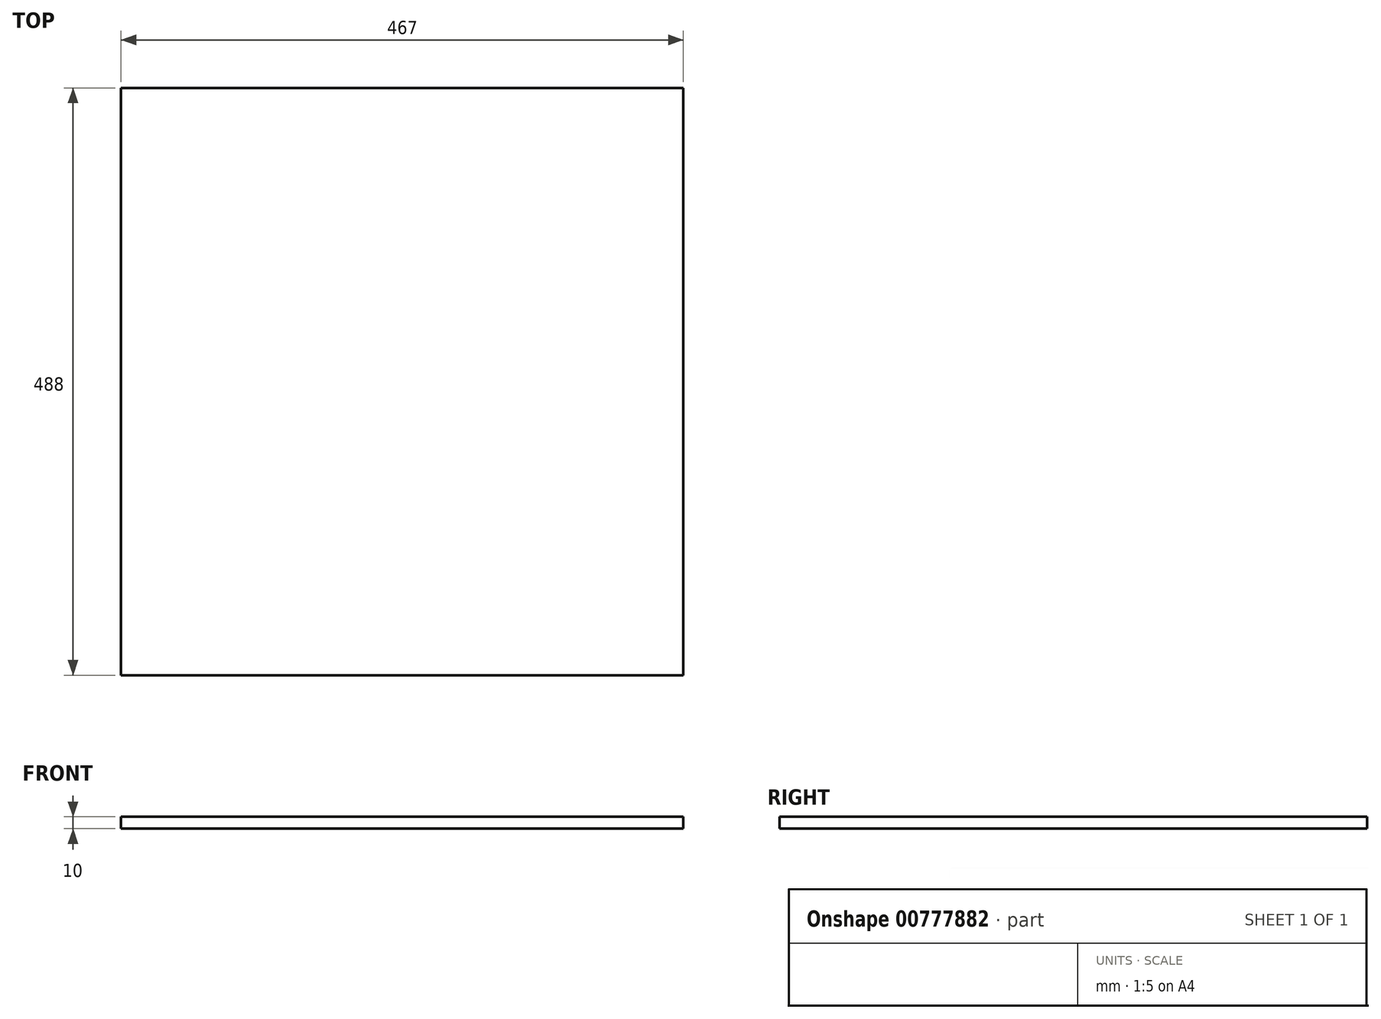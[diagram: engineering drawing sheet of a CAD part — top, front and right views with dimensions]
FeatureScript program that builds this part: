
annotation { "Feature Type Name" : "Feature", "Feature Type Description" : "" }
export const myFeature = defineFeature(function(context is Context, id is Id, definition is map)
    precondition{}
    {
        {
            var Q0;
            Q0=qCreatedBy(makeId("Top.planeOp"),FACE);
            var sketch = newSketch(context, id + "F0", { "sketchPlane" : qUnion([Q0])});
            skLineSegment(sketch, "E0.bottom", {"start": v(-233.5, 244) * mm, "end": v(233.5, 244) * mm});
            skLineSegment(sketch, "E0.top", {"start": v(-233.5, -244) * mm, "end": v(233.5, -244) * mm});
            skLineSegment(sketch, "E0.left", {"start": v(-233.5, 244) * mm, "end": v(-233.5, -244) * mm});
            skLineSegment(sketch, "E0.right", {"start": v(233.5, 244) * mm, "end": v(233.5, -244) * mm});
            skSolve(sketch);
        }
        {
            var Q0;
            Q0 = qSketchRegion(id + "F0", true);
            extrude(context, id + "F1", {"entities" : qUnion([Q0]), "endBound" : BoundingType.SYMMETRIC, "depth" : 10 * mm, "offsetDistance" : 25 * mm});
        }
    });
